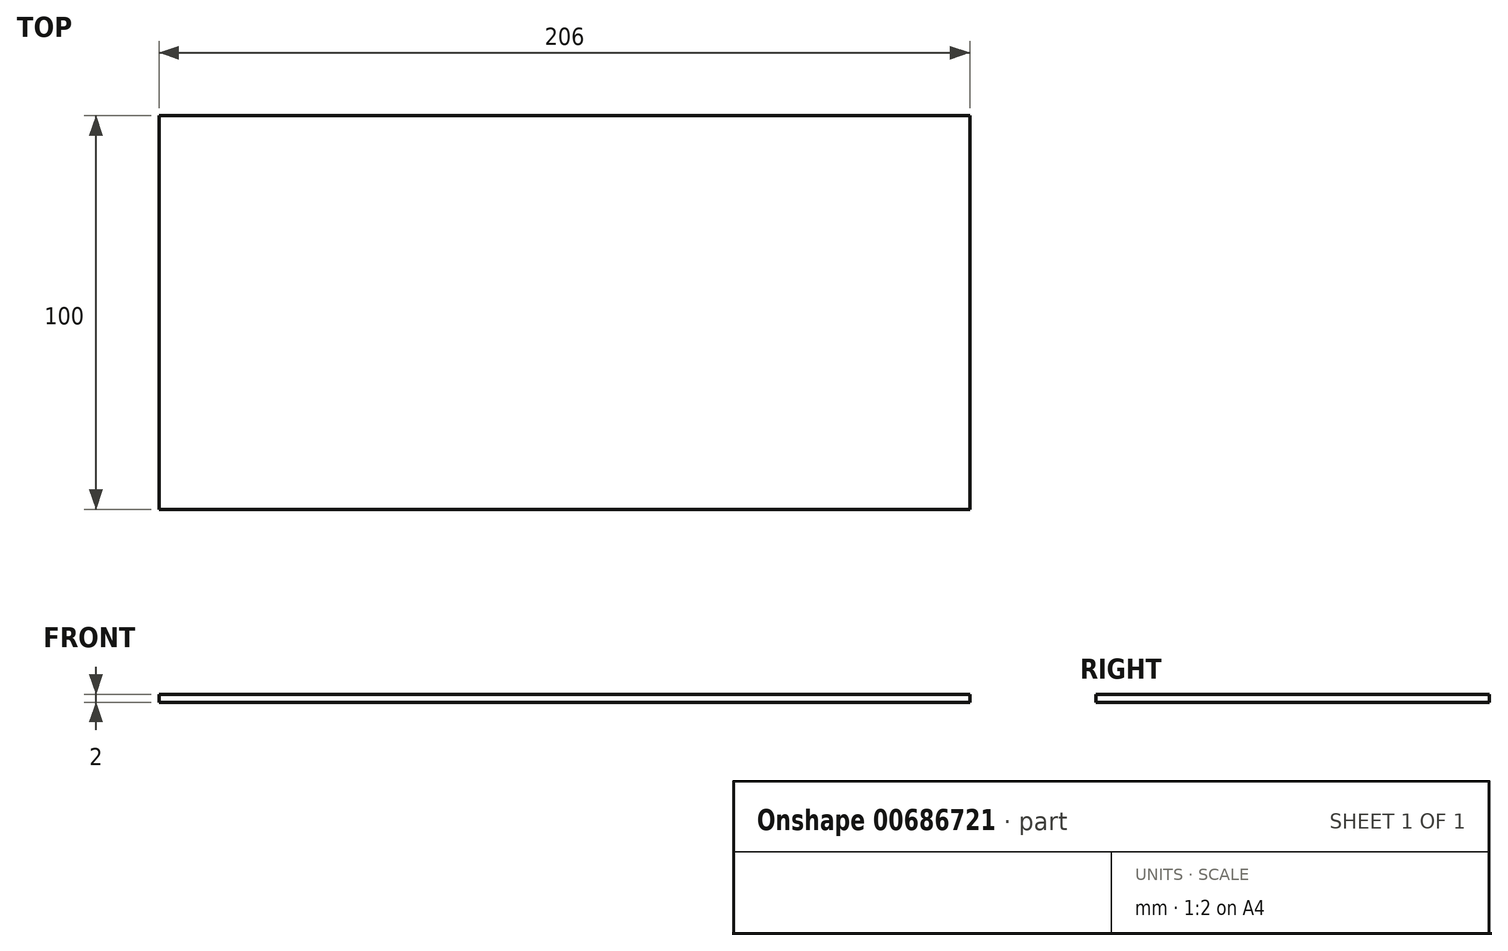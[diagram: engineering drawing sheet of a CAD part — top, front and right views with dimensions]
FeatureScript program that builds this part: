
annotation { "Feature Type Name" : "Feature", "Feature Type Description" : "" }
export const myFeature = defineFeature(function(context is Context, id is Id, definition is map)
    precondition{}
    {
        {
            var Q0;
            Q0=qCreatedBy(makeId("Top.planeOp"),FACE);
            var sketch = newSketch(context, id + "F0", { "sketchPlane" : qUnion([Q0])});
            skLineSegment(sketch, "E0.bottom", {"start": v(0, 0) * mm, "end": v(206, 0) * mm});
            skLineSegment(sketch, "E0.top", {"start": v(0, 100) * mm, "end": v(206, 100) * mm});
            skLineSegment(sketch, "E0.left", {"start": v(0, 0) * mm, "end": v(0, 100) * mm});
            skLineSegment(sketch, "E0.right", {"start": v(206, 0) * mm, "end": v(206, 100) * mm});
            skSolve(sketch);
        }
        {
            var Q0;
            Q0=makeQuery(id+"F0.imprint","IMPRINT",FACE,{"disambiguationData":[TD([[makeQuery(id+"F0.imprint","IMPRINT",EDGE,{"derivedFrom":sQuery(id+"F0.wireOp",EDGE,"E0.bottom")}),1.0]])]});
            extrude(context, id + "F1", {"entities" : qUnion([Q0]), "depth" : 2 * mm, "offsetDistance" : 25 * mm});
        }
    });
